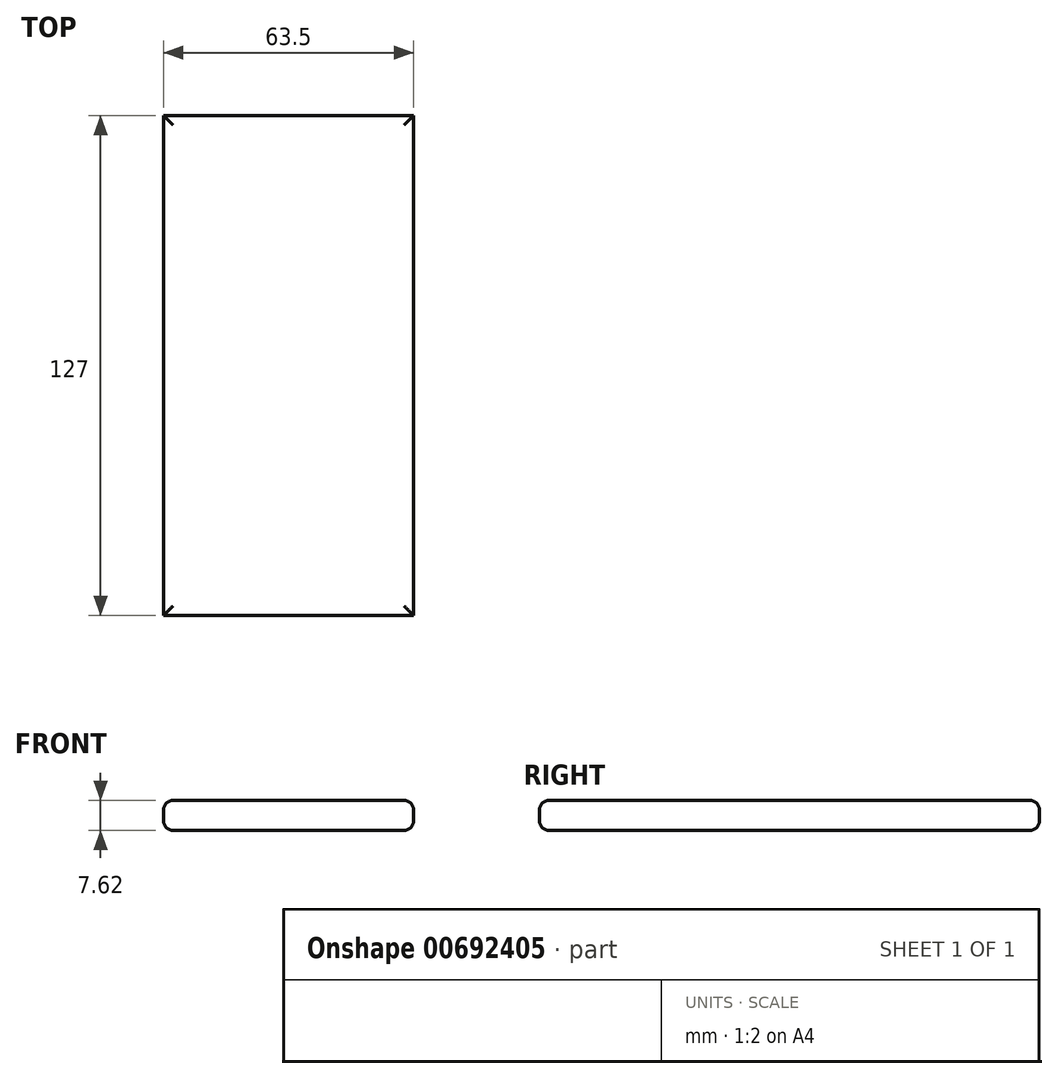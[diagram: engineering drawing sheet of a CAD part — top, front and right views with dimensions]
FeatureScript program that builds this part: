
annotation { "Feature Type Name" : "Feature", "Feature Type Description" : "" }
export const myFeature = defineFeature(function(context is Context, id is Id, definition is map)
    precondition{}
    {
        {
            var Q0;
            Q0=qCreatedBy(makeId("Top.planeOp"),FACE);
            var sketch = newSketch(context, id + "F0", { "sketchPlane" : qUnion([Q0])});
            skLineSegment(sketch, "E0.bottom", {"start": v(-31.75, 63.5) * mm, "end": v(31.75, 63.5) * mm});
            skLineSegment(sketch, "E0.top", {"start": v(-31.75, -63.5) * mm, "end": v(31.75, -63.5) * mm});
            skLineSegment(sketch, "E0.left", {"start": v(-31.75, 63.5) * mm, "end": v(-31.75, -63.5) * mm});
            skLineSegment(sketch, "E0.right", {"start": v(31.75, 63.5) * mm, "end": v(31.75, -63.5) * mm});
            skPoint(sketch, "E0.middle", {"position": v(0, 0) * mm});
            skSolve(sketch);
        }
        {
            var Q0;
            Q0=makeQuery(id+"F0.imprint","IMPRINT",FACE,{"disambiguationData":[TD([[makeQuery(id+"F0.imprint","IMPRINT",EDGE,{"derivedFrom":sQuery(id+"F0.wireOp",EDGE,"E0.bottom")}),-1.0]])]});
            extrude(context, id + "F1", {"entities" : qUnion([Q0]), "depth" : 7.62 * mm, "offsetDistance" : 25.4 * mm});
        }
        {
            var Q0;
            Q0=makeQuery(id+"F1.opExtrude","CAP_EDGE",EDGE,{"disambiguationData":[OSD([sQuery(id+"F0.wireOp",EDGE,"E0.left")])],"isStart":false});
            var Q1;
            Q1=makeQuery(id+"F1.opExtrude","CAP_EDGE",EDGE,{"disambiguationData":[OSD([sQuery(id+"F0.wireOp",EDGE,"E0.top")])],"isStart":false});
            var Q2;
            Q2=makeQuery(id+"F1.opExtrude","CAP_EDGE",EDGE,{"disambiguationData":[OSD([sQuery(id+"F0.wireOp",EDGE,"E0.right")])],"isStart":false});
            var Q3;
            Q3=makeQuery(id+"F1.opExtrude","CAP_EDGE",EDGE,{"disambiguationData":[OSD([sQuery(id+"F0.wireOp",EDGE,"E0.bottom")])],"isStart":false});
            var Q4;
            Q4=makeQuery(id+"F1.opExtrude","CAP_EDGE",EDGE,{"disambiguationData":[OSD([sQuery(id+"F0.wireOp",EDGE,"E0.bottom")])],"isStart":true});
            var Q5;
            Q5=makeQuery(id+"F1.opExtrude","CAP_EDGE",EDGE,{"disambiguationData":[OSD([sQuery(id+"F0.wireOp",EDGE,"E0.right")])],"isStart":true});
            var Q6;
            Q6=makeQuery(id+"F1.opExtrude","CAP_EDGE",EDGE,{"disambiguationData":[OSD([sQuery(id+"F0.wireOp",EDGE,"E0.top")])],"isStart":true});
            var Q7;
            Q7=makeQuery(id+"F1.opExtrude","CAP_EDGE",EDGE,{"disambiguationData":[OSD([sQuery(id+"F0.wireOp",EDGE,"E0.left")])],"isStart":true});
            fillet(context, id + "F2", {"entities" : qUnion([Q0, Q1, Q2, Q3, Q4, Q5, Q6, Q7]), "radius" : 2.45 * mm, "tangentPropagation" : true, "allowEdgeOverflow" : false});
        }
    });
